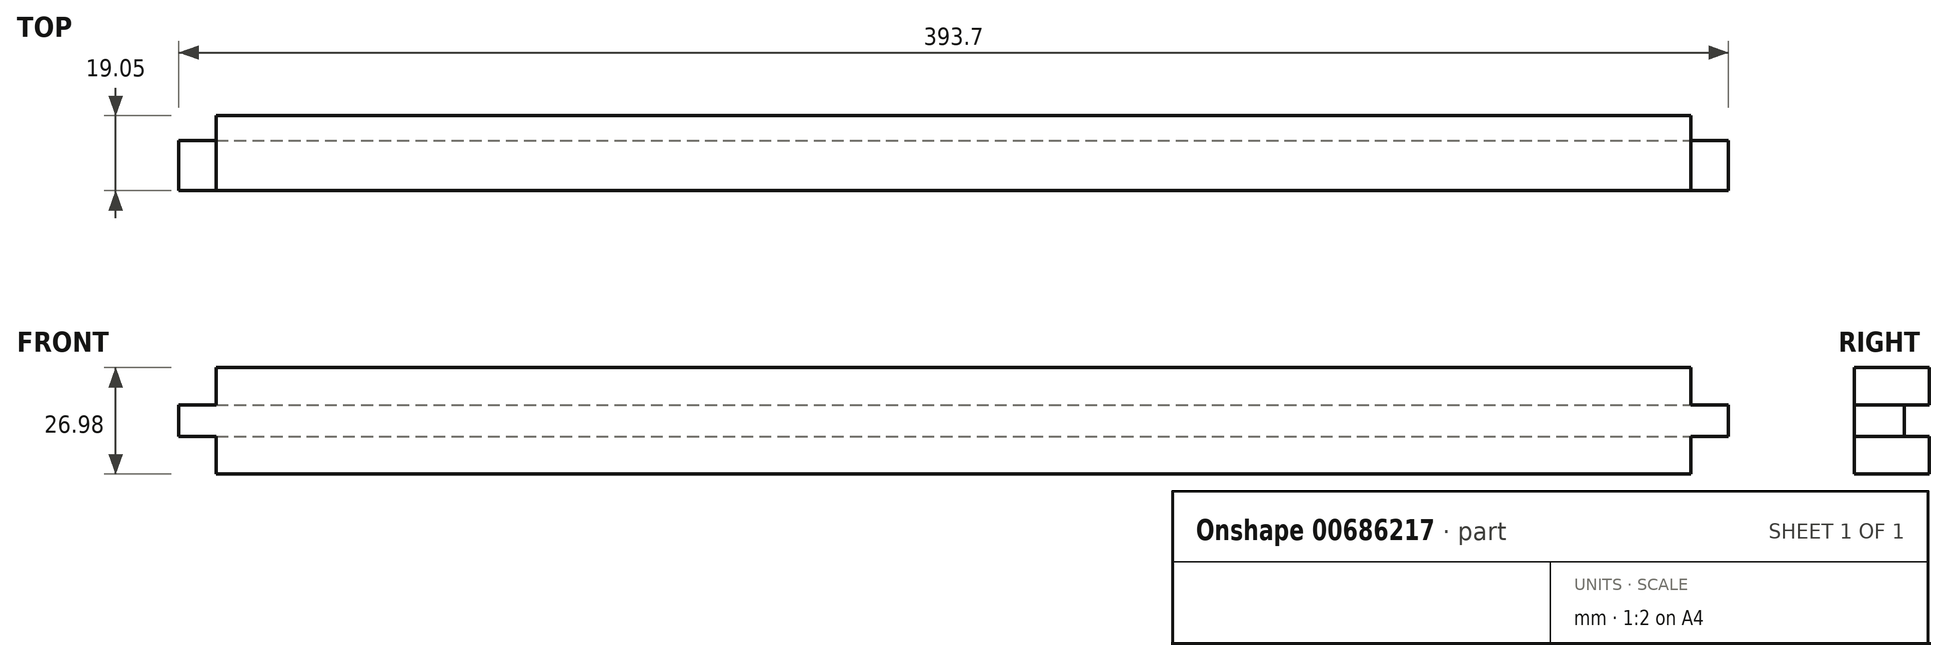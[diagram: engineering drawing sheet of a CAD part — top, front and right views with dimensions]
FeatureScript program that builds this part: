
annotation { "Feature Type Name" : "Feature", "Feature Type Description" : "" }
export const myFeature = defineFeature(function(context is Context, id is Id, definition is map)
    precondition{}
    {
        {
            var Q0;
            Q0=qCreatedBy(makeId("Front.planeOp"),FACE);
            var sketch = newSketch(context, id + "F0", { "sketchPlane" : qUnion([Q0])});
            skLineSegment(sketch, "E0", {"start": v(-196.85, -3.97) * mm, "end": v(-196.85, 3.97) * mm});
            skLineSegment(sketch, "E1", {"start": v(-196.85, 3.97) * mm, "end": v(-187.33, 3.97) * mm});
            skLineSegment(sketch, "E2", {"start": v(-187.33, 3.97) * mm, "end": v(-187.33, 13.5) * mm});
            skLineSegment(sketch, "E3", {"start": v(-187.33, 13.5) * mm, "end": v(187.33, 13.5) * mm});
            skLineSegment(sketch, "E4", {"start": v(187.33, 13.5) * mm, "end": v(187.33, 3.97) * mm});
            skLineSegment(sketch, "E5", {"start": v(187.33, 3.97) * mm, "end": v(196.85, 3.97) * mm});
            skLineSegment(sketch, "E6", {"start": v(196.85, 3.97) * mm, "end": v(196.85, -3.97) * mm});
            skLineSegment(sketch, "E7", {"start": v(-196.85, -3.97) * mm, "end": v(-187.33, -3.97) * mm});
            skLineSegment(sketch, "E8", {"start": v(-187.33, -3.97) * mm, "end": v(-187.33, -13.5) * mm});
            skLineSegment(sketch, "E9", {"start": v(-187.33, -13.5) * mm, "end": v(187.33, -13.5) * mm});
            skLineSegment(sketch, "E10", {"start": v(187.33, -13.5) * mm, "end": v(187.33, -3.97) * mm});
            skLineSegment(sketch, "E11", {"start": v(-187.33, 13.5) * mm, "end": v(187.33, -13.5) * mm, "construction": true});
            skLineSegment(sketch, "E12", {"start": v(187.33, -3.97) * mm, "end": v(196.85, -3.97) * mm});
            skSolve(sketch);
        }
        {
            var Q0;
            Q0=makeQuery(id+"F0.imprint","IMPRINT",FACE,{"disambiguationData":[TD([[makeQuery(id+"F0.imprint","IMPRINT",EDGE,{"derivedFrom":sQuery(id+"F0.wireOp",EDGE,"E0")}),-1.0]])]});
            extrude(context, id + "F1", {"entities" : qUnion([Q0]), "depth" : 19.05 * mm, "offsetDistance" : 25.4 * mm});
        }
        {
            var Q0;
            Q0=qCreatedBy(makeId("Right.planeOp"),FACE);
            var sketch = newSketch(context, id + "F2", { "sketchPlane" : qUnion([Q0])});
            skLineSegment(sketch, "E13.bottom", {"start": v(0, 3.97) * mm, "end": v(-6.35, 3.97) * mm});
            skLineSegment(sketch, "E13.top", {"start": v(0, -3.97) * mm, "end": v(-6.35, -3.97) * mm});
            skLineSegment(sketch, "E13.left", {"start": v(0, 3.97) * mm, "end": v(0, -3.97) * mm});
            skLineSegment(sketch, "E13.right", {"start": v(-6.35, 3.97) * mm, "end": v(-6.35, -3.97) * mm});
            skSolve(sketch);
        }
        {
            var Q0;
            Q0 = qSketchRegion(id + "F2", true);
            extrude(context, id + "F3", {"entities" : qUnion([Q0]), "operationType" : NewBodyOperationType.REMOVE, "endBound" : BoundingType.THROUGH_ALL, "oppositeDirection" : true, "depth" : 25.4 * mm, "offsetDistance" : 25.4 * mm, "hasSecondDirection" : true, "secondDirectionBound" : SecondDirectionBoundingType.THROUGH_ALL, "secondDirectionOppositeDirection" : false, "secondDirectionDepth" : 25.4 * mm});
        }
    });
